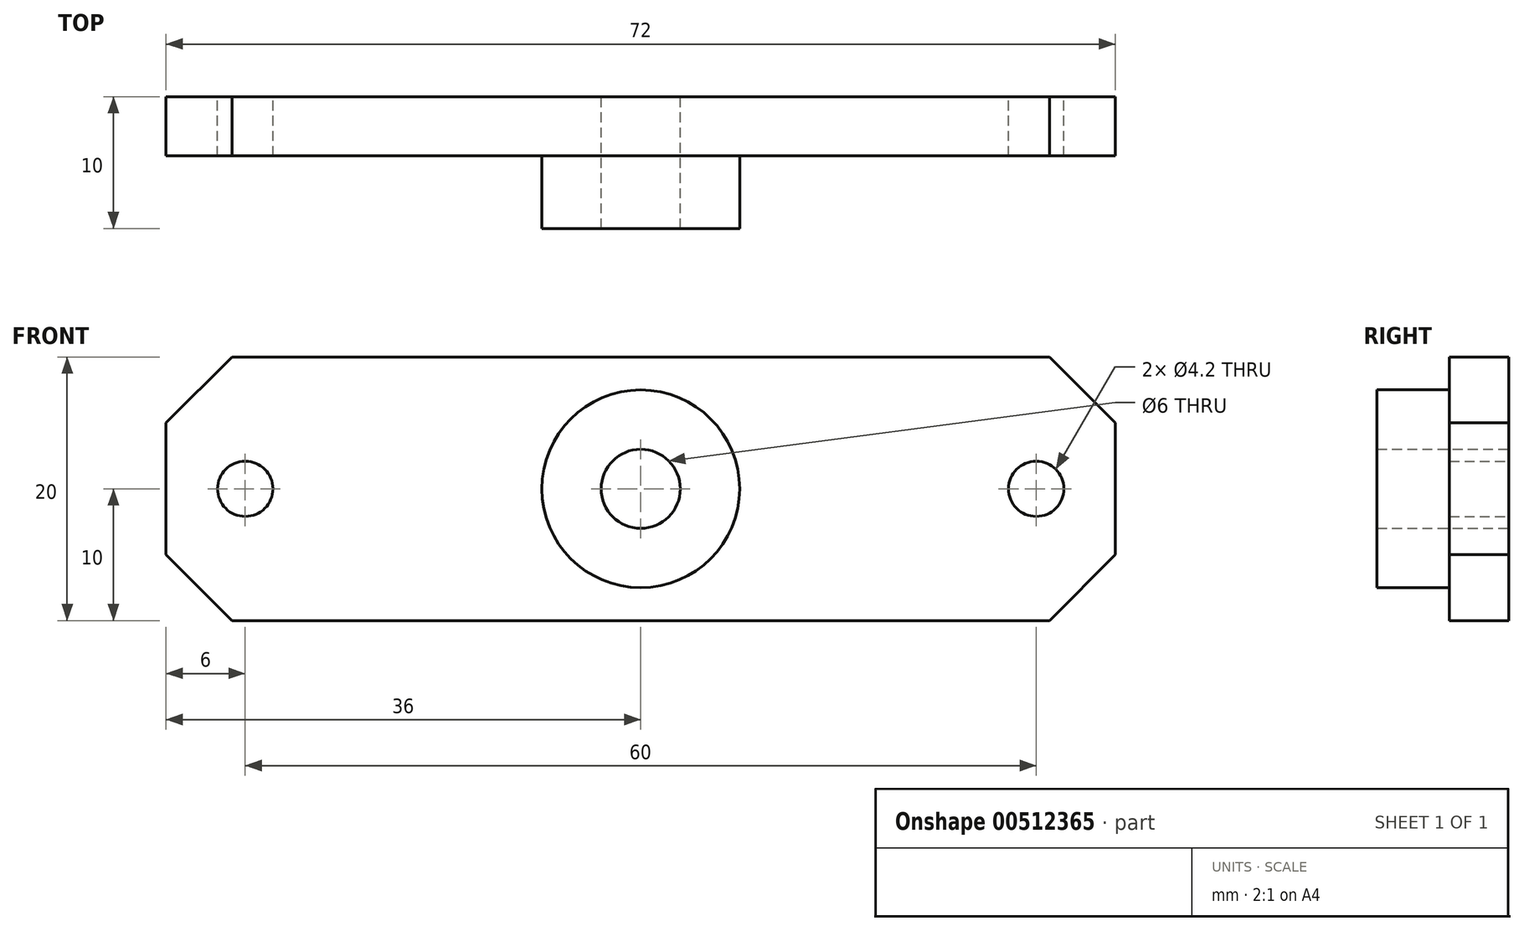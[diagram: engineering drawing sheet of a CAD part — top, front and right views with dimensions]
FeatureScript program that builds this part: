
annotation { "Feature Type Name" : "Feature", "Feature Type Description" : "" }
export const myFeature = defineFeature(function(context is Context, id is Id, definition is map)
    precondition{}
    {
        {
            var Q0;
            Q0=qCreatedBy(makeId("Front.planeOp"),FACE);
            var sketch = newSketch(context, id + "F0", { "sketchPlane" : qUnion([Q0])});
            skLineSegment(sketch, "E0.bottom", {"start": v(36, 10) * mm, "end": v(-36, 10) * mm});
            skLineSegment(sketch, "E0.top", {"start": v(36, -10) * mm, "end": v(-36, -10) * mm});
            skLineSegment(sketch, "E0.left", {"start": v(36, 10) * mm, "end": v(36, -10) * mm});
            skLineSegment(sketch, "E0.right", {"start": v(-36, 10) * mm, "end": v(-36, -10) * mm});
            skPoint(sketch, "E0.middle", {"position": v(0, 0) * mm});
            skCircle(sketch, "E1", {"center": v(0, 0) * mm, "radius": 3 * mm});
            skLineSegment(sketch, "E2", {"start": v(0, 32.36) * mm, "end": v(0, -28.18) * mm, "construction": true});
            skPoint(sketch, "E3.MirrorP", {"position": v(-30, -0.01) * mm});
            skPoint(sketch, "E4.MirrorP", {"position": v(30, -0.01) * mm});
            skSolve(sketch);
        }
        {
            var Q0;
            Q0 = qSketchRegion(id + "F0", true);
            extrude(context, id + "F1", {"entities" : qUnion([Q0]), "depth" : 4.5 * mm});
        }
        {
            var Q0;
            Q0=makeQuery(id+"F1.opExtrude","CAP_FACE",FACE,{"disambiguationData":[OSD([sQuery(id+"F0.wireOp",EDGE,"E0.bottom"),sQuery(id+"F0.wireOp",EDGE,"E0.top"),sQuery(id+"F0.wireOp",EDGE,"E0.left"),sQuery(id+"F0.wireOp",EDGE,"E0.right"),sQuery(id+"F0.wireOp",EDGE,"E1"),sQuery(id+"F0.wireOp",EDGE,"ENy42JfF-6w3e-OXzw-JDkE-4kl2GYuJj7oi"),sQuery(id+"F0.wireOp",EDGE,"80a0704a-bb5c-43a5-97d3-b2e101dcfcec0.MirrorC")])],"isStart":false});
            var sketch = newSketch(context, id + "F2", { "sketchPlane" : qUnion([Q0])});
            skCircle(sketch, "E5", {"center": v(0, 0) * mm, "radius": 7.5 * mm});
            skSolve(sketch);
        }
        {
            var Q0;
            Q0=makeQuery(id+"F2.imprint","IMPRINT",FACE,{"disambiguationData":[TD([[makeQuery(id+"F2.imprint","IMPRINT",EDGE,{"derivedFrom":sQuery(id+"F2.wireOp",EDGE,"E5")}),1.0]])]});
            extrude(context, id + "F3", {"entities" : qUnion([Q0]), "operationType" : NewBodyOperationType.ADD, "depth" : 5.5 * mm});
        }
        {
            var Q0;
            Q0=makeQuery(id+"F1.opExtrude","SWEPT_EDGE",EDGE,{"disambiguationData":[OSD([sQuery(id+"F0.wireOp",EDGE,"E0.bottom"),sQuery(id+"F0.wireOp",EDGE,"E0.left")])]});
            var Q1;
            Q1=makeQuery(id+"F1.opExtrude","SWEPT_EDGE",EDGE,{"disambiguationData":[OSD([sQuery(id+"F0.wireOp",EDGE,"E0.top"),sQuery(id+"F0.wireOp",EDGE,"E0.left")])]});
            var Q2;
            Q2=makeQuery(id+"F1.opExtrude","SWEPT_EDGE",EDGE,{"disambiguationData":[OSD([sQuery(id+"F0.wireOp",EDGE,"E0.bottom"),sQuery(id+"F0.wireOp",EDGE,"E0.right")])]});
            var Q3;
            Q3=makeQuery(id+"F1.opExtrude","SWEPT_EDGE",EDGE,{"disambiguationData":[OSD([sQuery(id+"F0.wireOp",EDGE,"E0.top"),sQuery(id+"F0.wireOp",EDGE,"E0.right")])]});
            chamfer(context, id + "F4", {"entities" : qUnion([Q0, Q1, Q2, Q3]), "width" : 5 * mm, "tangentPropagation" : true});
        }
        {
            var Q0;
            Q0=makeQuery(id+"F1.opExtrude","CAP_FACE",FACE,{"disambiguationData":[OSD([sQuery(id+"F0.wireOp",EDGE,"E0.bottom"),sQuery(id+"F0.wireOp",EDGE,"E0.top"),sQuery(id+"F0.wireOp",EDGE,"E0.left"),sQuery(id+"F0.wireOp",EDGE,"E0.right"),sQuery(id+"F0.wireOp",EDGE,"E1")])],"isStart":true});
            var sketch = newSketch(context, id + "F5", { "sketchPlane" : qUnion([Q0])});
            skCircle(sketch, "E6", {"center": v(-30, 0) * mm, "radius": 2.09 * mm});
            skCircle(sketch, "E7.MirrorC", {"center": v(30, 0) * mm, "radius": 2.09 * mm});
            skSolve(sketch);
        }
        {
            var Q0;
            Q0=sQuery(id+"F5.wireOp",VERTEX,"E6.center");
            var Q1;
            Q1=sQuery(id+"F5.wireOp",VERTEX,"E7.MirrorC.center");
            var Q2;
            Q2=makeQuery(id+"F1.opExtrude","SWEPT_BODY",BODY,{"disambiguationData":[OSD([sQuery(id+"F0.wireOp",EDGE,"E0.bottom"),sQuery(id+"F0.wireOp",EDGE,"E0.top"),sQuery(id+"F0.wireOp",EDGE,"E0.left"),sQuery(id+"F0.wireOp",EDGE,"E0.right"),sQuery(id+"F0.wireOp",EDGE,"E1")])]});
            hole(context, id + "F6", {"style" : HoleStyle.SIMPLE, "endStyle" : HoleEndStyle.THROUGH, "standardTappedOrClearance" : lookupTablePath({ "standard" : "ISO", "engagement" : "75%", "pitch" : "0.8 mm", "size" : "M5", "type" : "Tapped" }), "standardBlindInLast" : lookupTablePath({ "standard" : "ISO", "engagement" : "75%", "pitch" : "0.8 mm", "size" : "M5", "type" : "Tapped" }), "holeDiameter" : 4.2 * mm, "showTappedDepth" : true, "isTappedThrough" : true, "tappedDepth" : 12 * mm, "tapClearance" : 3, "startFromSketch" : true, "locations" : qUnion([Q0, Q1]), "scope" : qUnion([Q2]), "majorDiameter" : 5 * mm});
        }
    });
